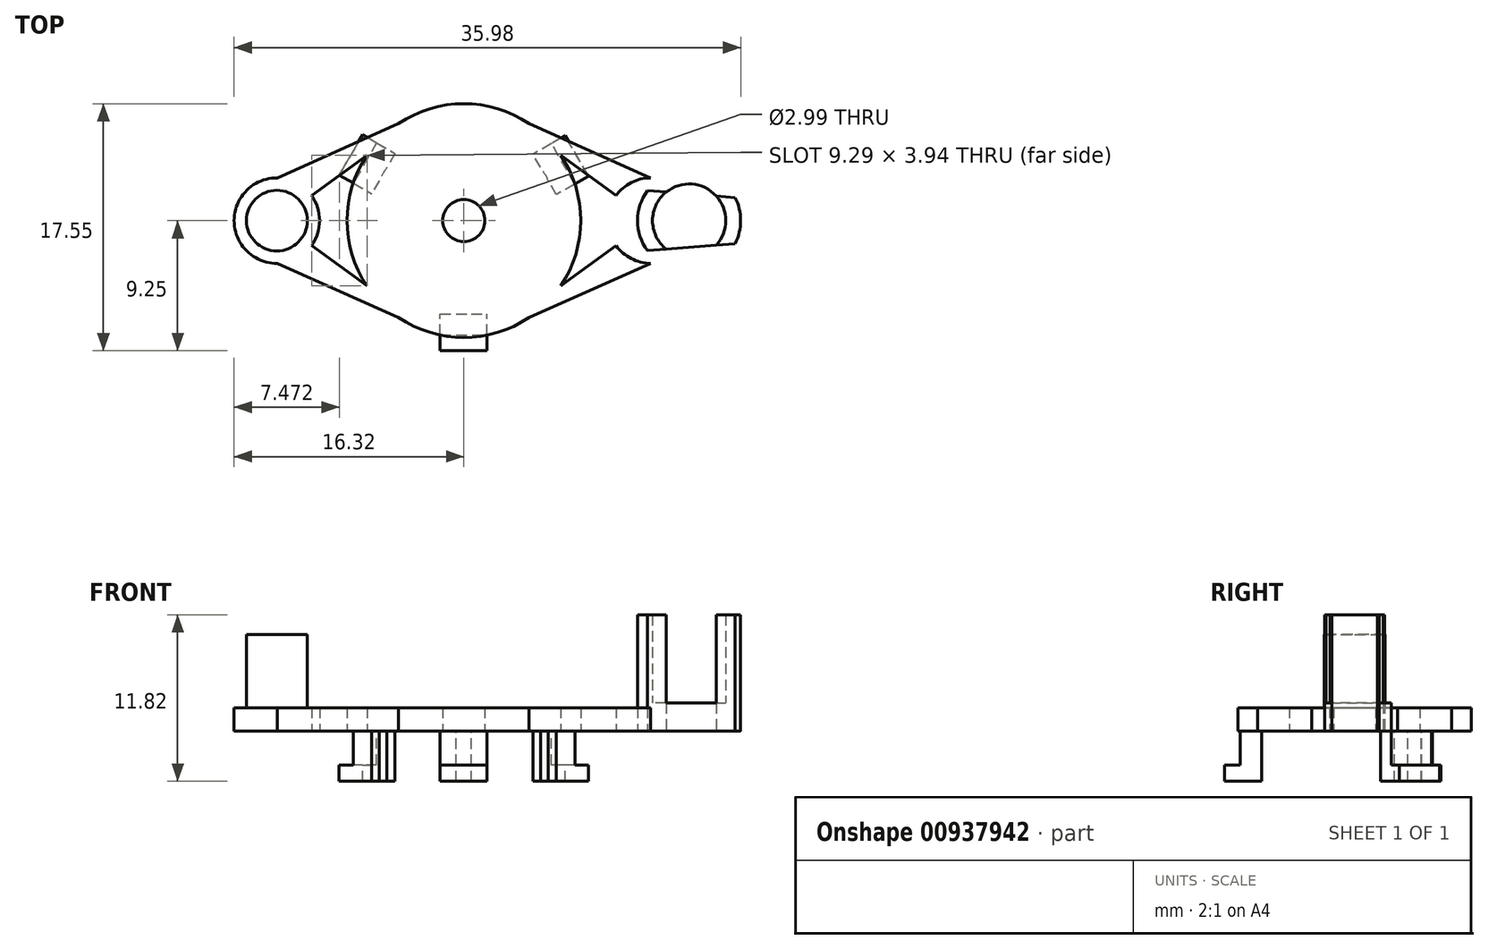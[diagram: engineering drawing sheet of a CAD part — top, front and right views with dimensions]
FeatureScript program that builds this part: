
annotation { "Feature Type Name" : "Feature", "Feature Type Description" : "" }
export const myFeature = defineFeature(function(context is Context, id is Id, definition is map)
    precondition{}
    {
        {
            var Q0;
            Q0=qCreatedBy(makeId("Top.planeOp"),FACE);
            var sketch = newSketch(context, id + "F0", { "sketchPlane" : qUnion([Q0])});
            skPoint(sketch, "E0.middle", {"position": v(0, 0) * mm});
            skCircle(sketch, "E1", {"center": v(-16, 0) * mm, "radius": 2.6 * mm});
            skCircle(sketch, "E2.MirrorC", {"center": v(16, 0) * mm, "radius": 2.6 * mm});
            skCircle(sketch, "E3", {"center": v(0, 0) * mm, "radius": 1.8 * mm});
            skCircle(sketch, "E4", {"center": v(-16, 0) * mm, "radius": 3.66 * mm});
            skCircle(sketch, "E5.MirrorC", {"center": v(16, 0) * mm, "radius": 3.66 * mm});
            skCircle(sketch, "E6", {"center": v(0, 0) * mm, "radius": 10 * mm});
            skLineSegment(sketch, "E7", {"start": v(-19.27, 1.63) * mm, "end": v(-9.7, 2.4) * mm});
            skLineSegment(sketch, "E8.MirrorCS", {"start": v(-19.27, -1.63) * mm, "end": v(-9.7, -2.4) * mm});
            skLineSegment(sketch, "E9.MirrorCS", {"start": v(19.27, 1.63) * mm, "end": v(9.7, 2.4) * mm});
            skLineSegment(sketch, "E10.MirrorCS", {"start": v(19.27, -1.63) * mm, "end": v(9.7, -2.4) * mm});
            skLineSegment(sketch, "E11", {"start": v(-15.97, 3.66) * mm, "end": v(-5.58, 8.3) * mm});
            skLineSegment(sketch, "E12", {"start": v(-13.03, 2.14) * mm, "end": v(-8.29, 5.6) * mm});
            skLineSegment(sketch, "E13.MirrorCS", {"start": v(-13.03, -2.14) * mm, "end": v(-8.29, -5.6) * mm});
            skLineSegment(sketch, "E14.MirrorCS", {"start": v(-15.97, -3.66) * mm, "end": v(-5.58, -8.3) * mm});
            skLineSegment(sketch, "E15.MirrorCS", {"start": v(13.03, 2.14) * mm, "end": v(8.29, 5.6) * mm});
            skLineSegment(sketch, "E16.MirrorCS", {"start": v(15.97, 3.66) * mm, "end": v(5.58, 8.3) * mm});
            skLineSegment(sketch, "E17.MirrorCS", {"start": v(15.97, -3.66) * mm, "end": v(5.58, -8.3) * mm});
            skLineSegment(sketch, "E18.MirrorCS", {"start": v(13.03, -2.14) * mm, "end": v(8.29, -5.6) * mm});
            skCircle(sketch, "E19", {"center": v(0, 0) * mm, "radius": 8 * mm});
            skLineSegment(sketch, "E20.bottom", {"start": v(-2.04, -9.79) * mm, "end": v(1.96, -9.79) * mm});
            skLineSegment(sketch, "E20.top", {"start": v(-2.04, -7.97) * mm, "end": v(1.96, -7.97) * mm});
            skLineSegment(sketch, "E20.left", {"start": v(-2.04, -9.79) * mm, "end": v(-2.04, -7.97) * mm});
            skLineSegment(sketch, "E20.right", {"start": v(1.96, -9.79) * mm, "end": v(1.96, -7.97) * mm});
            skLineSegment(sketch, "E21.1.0", {"start": v(9.5, 3.13) * mm, "end": v(7.5, 6.6) * mm});
            skLineSegment(sketch, "E21.1.1", {"start": v(7.5, 6.6) * mm, "end": v(5.92, 5.68) * mm});
            skLineSegment(sketch, "E21.1.2", {"start": v(7.92, 2.22) * mm, "end": v(5.92, 5.68) * mm});
            skLineSegment(sketch, "E21.1.3", {"start": v(9.5, 3.13) * mm, "end": v(7.92, 2.22) * mm});
            skLineSegment(sketch, "E21.2.0", {"start": v(-7.46, 6.66) * mm, "end": v(-9.46, 3.2) * mm});
            skLineSegment(sketch, "E21.2.1", {"start": v(-9.46, 3.2) * mm, "end": v(-7.89, 2.29) * mm});
            skLineSegment(sketch, "E21.2.2", {"start": v(-5.89, 5.75) * mm, "end": v(-7.89, 2.29) * mm});
            skLineSegment(sketch, "E21.2.3", {"start": v(-7.46, 6.66) * mm, "end": v(-5.89, 5.75) * mm});
            skSolve(sketch);
        }
        {
            var Q0;
            {var subQ0=sQuery(id+"F0.wireOp",EDGE,"E11");Q0=makeQuery(id+"F0.imprint","IMPRINT",FACE,{"disambiguationData":[TD([[makeQuery(id+"F0.imprint","IMPRINT",EDGE,{"derivedFrom":subQ0}),-1.0]])]});}
            var Q1;
            Q1=makeQuery(id+"F0.imprint","IMPRINT",FACE,{"disambiguationData":[TD([[makeQuery(id+"F0.imprint","IMPRINT",EDGE,{"derivedFrom":sQuery(id+"F0.wireOp",EDGE,"E3")}),-1.0]])]});
            var Q2;
            {var subQ0=sQuery(id+"F0.wireOp",EDGE,"E13.MirrorCS");Q2=makeQuery(id+"F0.imprint","IMPRINT",FACE,{"disambiguationData":[TD([[makeQuery(id+"F0.imprint","IMPRINT",EDGE,{"derivedFrom":subQ0}),-1.0]])]});}
            var Q3;
            {var subQ0=sQuery(id+"F0.wireOp",EDGE,"E8.MirrorCS");var subQ3=sQuery(id+"F0.wireOp",EDGE,"E1");var subQ4=makeQuery(id+"F0.imprint","INTERSECT",VERTEX,{"disambiguationData":[OD(0.0)],"derivedFrom":[subQ3,subQ0]});Q3=makeQuery(id+"F0.imprint","IMPRINT",FACE,{"disambiguationData":[TD([[makeQuery(id+"F0.imprint","IMPRINT",EDGE,{"disambiguationData":[TD([[subQ4,-1.0]])],"derivedFrom":subQ3}),-1.0]])]});}
            var Q4;
            {var subQ0=sQuery(id+"F0.wireOp",EDGE,"E7");var subQ1=sQuery(id+"F0.wireOp",EDGE,"E1");var subQ2=makeQuery(id+"F0.imprint","INTERSECT",VERTEX,{"disambiguationData":[OD(0.0)],"derivedFrom":[subQ1,subQ0]});Q4=makeQuery(id+"F0.imprint","IMPRINT",FACE,{"disambiguationData":[TD([[makeQuery(id+"F0.imprint","IMPRINT",EDGE,{"disambiguationData":[TD([[subQ2,-1.0]])],"derivedFrom":subQ1}),-1.0]])]});}
            var Q5;
            {var subQ0=sQuery(id+"F0.wireOp",EDGE,"E7");var subQ3=sQuery(id+"F0.wireOp",EDGE,"E1");var subQ4=makeQuery(id+"F0.imprint","INTERSECT",VERTEX,{"disambiguationData":[OD(0.0)],"derivedFrom":[subQ3,subQ0]});Q5=makeQuery(id+"F0.imprint","IMPRINT",FACE,{"disambiguationData":[TD([[makeQuery(id+"F0.imprint","IMPRINT",EDGE,{"disambiguationData":[TD([[subQ4,1.0]])],"derivedFrom":subQ3}),-1.0]])]});}
            var Q6;
            {var subQ0=sQuery(id+"F0.wireOp",EDGE,"E7");var subQ1=sQuery(id+"F0.wireOp",EDGE,"E1");var subQ2=makeQuery(id+"F0.imprint","INTERSECT",VERTEX,{"disambiguationData":[OD(1.0)],"derivedFrom":[subQ1,subQ0]});Q6=makeQuery(id+"F0.imprint","IMPRINT",FACE,{"disambiguationData":[TD([[makeQuery(id+"F0.imprint","IMPRINT",EDGE,{"disambiguationData":[TD([[subQ2,1.0]])],"derivedFrom":subQ1}),-1.0]])]});}
            var Q7;
            {var subQ0=sQuery(id+"F0.wireOp",EDGE,"E17.MirrorCS");Q7=makeQuery(id+"F0.imprint","IMPRINT",FACE,{"disambiguationData":[TD([[makeQuery(id+"F0.imprint","IMPRINT",EDGE,{"derivedFrom":subQ0}),-1.0]])]});}
            var Q8;
            {var subQ0=sQuery(id+"F0.wireOp",EDGE,"E15.MirrorCS");Q8=makeQuery(id+"F0.imprint","IMPRINT",FACE,{"disambiguationData":[TD([[makeQuery(id+"F0.imprint","IMPRINT",EDGE,{"derivedFrom":subQ0}),-1.0]])]});}
            var Q9;
            {var subQ0=sQuery(id+"F0.wireOp",EDGE,"E9.MirrorCS");var subQ3=sQuery(id+"F0.wireOp",EDGE,"E2.MirrorC");var subQ4=makeQuery(id+"F0.imprint","INTERSECT",VERTEX,{"disambiguationData":[OD(0.0)],"derivedFrom":[subQ3,subQ0]});Q9=makeQuery(id+"F0.imprint","IMPRINT",FACE,{"disambiguationData":[TD([[makeQuery(id+"F0.imprint","IMPRINT",EDGE,{"disambiguationData":[TD([[subQ4,1.0]])],"derivedFrom":subQ3}),1.0]])]});}
            var Q10;
            {var subQ0=sQuery(id+"F0.wireOp",EDGE,"E9.MirrorCS");var subQ1=sQuery(id+"F0.wireOp",EDGE,"E2.MirrorC");var subQ2=makeQuery(id+"F0.imprint","INTERSECT",VERTEX,{"disambiguationData":[OD(1.0)],"derivedFrom":[subQ1,subQ0]});Q10=makeQuery(id+"F0.imprint","IMPRINT",FACE,{"disambiguationData":[TD([[makeQuery(id+"F0.imprint","IMPRINT",EDGE,{"disambiguationData":[TD([[subQ2,1.0]])],"derivedFrom":subQ1}),1.0]])]});}
            var Q11;
            {var subQ0=sQuery(id+"F0.wireOp",EDGE,"E10.MirrorCS");var subQ3=sQuery(id+"F0.wireOp",EDGE,"E2.MirrorC");var subQ4=makeQuery(id+"F0.imprint","INTERSECT",VERTEX,{"disambiguationData":[OD(0.0)],"derivedFrom":[subQ3,subQ0]});Q11=makeQuery(id+"F0.imprint","IMPRINT",FACE,{"disambiguationData":[TD([[makeQuery(id+"F0.imprint","IMPRINT",EDGE,{"disambiguationData":[TD([[subQ4,-1.0]])],"derivedFrom":subQ3}),1.0]])]});}
            var Q12;
            {var subQ0=sQuery(id+"F0.wireOp",EDGE,"E9.MirrorCS");var subQ1=sQuery(id+"F0.wireOp",EDGE,"E2.MirrorC");var subQ2=makeQuery(id+"F0.imprint","INTERSECT",VERTEX,{"disambiguationData":[OD(0.0)],"derivedFrom":[subQ1,subQ0]});Q12=makeQuery(id+"F0.imprint","IMPRINT",FACE,{"disambiguationData":[TD([[makeQuery(id+"F0.imprint","IMPRINT",EDGE,{"disambiguationData":[TD([[subQ2,-1.0]])],"derivedFrom":subQ1}),1.0]])]});}
            var Q13;
            {var subQ0=sQuery(id+"F0.wireOp",EDGE,"E6");var subQ8=makeQuery(id+"F0.imprint","INTERSECT",VERTEX,{"derivedFrom":[subQ0,sQuery(id+"F0.wireOp",EDGE,"E9.MirrorCS")]});Q13=makeQuery(id+"F0.imprint","IMPRINT",FACE,{"disambiguationData":[TD([[makeQuery(id+"F0.imprint","IMPRINT",EDGE,{"disambiguationData":[TD([[subQ8,-1.0]])],"derivedFrom":subQ0}),1.0]])]});}
            var Q14;
            {var subQ0=sQuery(id+"F0.wireOp",EDGE,"E20.left");Q14=makeQuery(id+"F0.imprint","IMPRINT",FACE,{"disambiguationData":[TD([[makeQuery(id+"F0.imprint","IMPRINT",EDGE,{"derivedFrom":subQ0}),1.0]])]});}
            var Q15;
            {var subQ7=sQuery(id+"F0.wireOp",EDGE,"E21.1.3");Q15=makeQuery(id+"F0.imprint","IMPRINT",FACE,{"disambiguationData":[TD([[makeQuery(id+"F0.imprint","IMPRINT",EDGE,{"derivedFrom":subQ7}),1.0]])]});}
            var Q16;
            {var subQ5=sQuery(id+"F0.wireOp",EDGE,"E21.2.3");Q16=makeQuery(id+"F0.imprint","IMPRINT",FACE,{"disambiguationData":[TD([[makeQuery(id+"F0.imprint","IMPRINT",EDGE,{"derivedFrom":subQ5}),1.0]])]});}
            var Q17;
            {var subQ0=sQuery(id+"F0.wireOp",EDGE,"E20.bottom");var subQ1=sQuery(id+"F0.wireOp",EDGE,"E6");var subQ3=makeQuery(id+"F0.imprint","INTERSECT",VERTEX,{"derivedFrom":[subQ1,subQ0]});Q17=makeQuery(id+"F0.imprint","IMPRINT",FACE,{"disambiguationData":[TD([[makeQuery(id+"F0.imprint","IMPRINT",EDGE,{"disambiguationData":[TD([[subQ3,1.0]])],"derivedFrom":subQ1}),1.0]])]});}
            var Q18;
            {var subQ0=sQuery(id+"F0.wireOp",EDGE,"E21.1.0");var subQ1=sQuery(id+"F0.wireOp",EDGE,"E6");var subQ3=makeQuery(id+"F0.imprint","INTERSECT",VERTEX,{"derivedFrom":[subQ1,subQ0]});Q18=makeQuery(id+"F0.imprint","IMPRINT",FACE,{"disambiguationData":[TD([[makeQuery(id+"F0.imprint","IMPRINT",EDGE,{"disambiguationData":[TD([[subQ3,1.0]])],"derivedFrom":subQ1}),1.0]])]});}
            var Q19;
            {var subQ0=sQuery(id+"F0.wireOp",EDGE,"E21.2.0");var subQ1=sQuery(id+"F0.wireOp",EDGE,"E6");var subQ3=makeQuery(id+"F0.imprint","INTERSECT",VERTEX,{"derivedFrom":[subQ1,subQ0]});Q19=makeQuery(id+"F0.imprint","IMPRINT",FACE,{"disambiguationData":[TD([[makeQuery(id+"F0.imprint","IMPRINT",EDGE,{"disambiguationData":[TD([[subQ3,1.0]])],"derivedFrom":subQ1}),1.0]])]});}
            var Q20;
            {var subQ0=sQuery(id+"F0.wireOp",EDGE,"E20.left");Q20=makeQuery(id+"F0.imprint","IMPRINT",FACE,{"disambiguationData":[TD([[makeQuery(id+"F0.imprint","IMPRINT",EDGE,{"derivedFrom":subQ0}),-1.0]])]});}
            var Q21;
            {var subQ5=sQuery(id+"F0.wireOp",EDGE,"E21.2.3");Q21=makeQuery(id+"F0.imprint","IMPRINT",FACE,{"disambiguationData":[TD([[makeQuery(id+"F0.imprint","IMPRINT",EDGE,{"derivedFrom":subQ5}),-1.0]])]});}
            var Q22;
            {var subQ5=sQuery(id+"F0.wireOp",EDGE,"E21.1.3");Q22=makeQuery(id+"F0.imprint","IMPRINT",FACE,{"disambiguationData":[TD([[makeQuery(id+"F0.imprint","IMPRINT",EDGE,{"derivedFrom":subQ5}),-1.0]])]});}
            var Q23;
            {var subQ0=sQuery(id+"F0.wireOp",EDGE,"E20.top");var subQ1=sQuery(id+"F0.wireOp",EDGE,"E19");var subQ2=makeQuery(id+"F0.imprint","INTERSECT",VERTEX,{"disambiguationData":[OD(0.0)],"derivedFrom":[subQ1,subQ0]});Q23=makeQuery(id+"F0.imprint","IMPRINT",FACE,{"disambiguationData":[TD([[makeQuery(id+"F0.imprint","IMPRINT",EDGE,{"disambiguationData":[TD([[subQ2,-1.0]])],"derivedFrom":subQ1}),1.0]])]});}
            var Q24;
            {var subQ0=sQuery(id+"F0.wireOp",EDGE,"E21.2.2");var subQ1=sQuery(id+"F0.wireOp",EDGE,"E19");var subQ2=makeQuery(id+"F0.imprint","INTERSECT",VERTEX,{"disambiguationData":[OD(0.0)],"derivedFrom":[subQ1,subQ0]});Q24=makeQuery(id+"F0.imprint","IMPRINT",FACE,{"disambiguationData":[TD([[makeQuery(id+"F0.imprint","IMPRINT",EDGE,{"disambiguationData":[TD([[subQ2,-1.0]])],"derivedFrom":subQ1}),1.0]])]});}
            var Q25;
            {var subQ0=sQuery(id+"F0.wireOp",EDGE,"E21.1.2");var subQ1=sQuery(id+"F0.wireOp",EDGE,"E19");var subQ2=makeQuery(id+"F0.imprint","INTERSECT",VERTEX,{"disambiguationData":[OD(0.0)],"derivedFrom":[subQ1,subQ0]});Q25=makeQuery(id+"F0.imprint","IMPRINT",FACE,{"disambiguationData":[TD([[makeQuery(id+"F0.imprint","IMPRINT",EDGE,{"disambiguationData":[TD([[subQ2,1.0]])],"derivedFrom":subQ1}),1.0]])]});}
            extrude(context, id + "F1", {"entities" : qUnion([Q0, Q1, Q2, Q3, Q4, Q5, Q6, Q7, Q8, Q9, Q10, Q11, Q12, Q13, Q14, Q15, Q16, Q17, Q18, Q19, Q20, Q21, Q22, Q23, Q24, Q25]), "depth" : 2 * mm, "offsetDistance" : 25 * mm});
        }
        {
            var Q0;
            Q0=makeQuery(id+"F0.imprint","IMPRINT",FACE,{"disambiguationData":[TD([[makeQuery(id+"F0.imprint","IMPRINT",EDGE,{"derivedFrom":sQuery(id+"F0.wireOp",EDGE,"E1")}),1.0]])]});
            var Q1;
            Q1=makeQuery(id+"F0.imprint","IMPRINT",FACE,{"disambiguationData":[TD([[makeQuery(id+"F0.imprint","IMPRINT",EDGE,{"derivedFrom":sQuery(id+"F0.wireOp",EDGE,"E2.MirrorC")}),-1.0]])]});
            var Q2;
            {var subQ0=sQuery(id+"F0.wireOp",EDGE,"E7");var subQ1=sQuery(id+"F0.wireOp",EDGE,"E1");var subQ2=makeQuery(id+"F0.imprint","INTERSECT",VERTEX,{"disambiguationData":[OD(0.0)],"derivedFrom":[subQ1,subQ0]});Q2=makeQuery(id+"F0.imprint","IMPRINT",FACE,{"disambiguationData":[TD([[makeQuery(id+"F0.imprint","IMPRINT",EDGE,{"disambiguationData":[TD([[subQ2,1.0]])],"derivedFrom":subQ1}),1.0]])]});}
            var Q3;
            {var subQ0=sQuery(id+"F0.wireOp",EDGE,"E8.MirrorCS");var subQ1=sQuery(id+"F0.wireOp",EDGE,"E1");var subQ2=makeQuery(id+"F0.imprint","INTERSECT",VERTEX,{"disambiguationData":[OD(0.0)],"derivedFrom":[subQ1,subQ0]});Q3=makeQuery(id+"F0.imprint","IMPRINT",FACE,{"disambiguationData":[TD([[makeQuery(id+"F0.imprint","IMPRINT",EDGE,{"disambiguationData":[TD([[subQ2,-1.0]])],"derivedFrom":subQ1}),1.0]])]});}
            var Q4;
            {var subQ0=sQuery(id+"F0.wireOp",EDGE,"E10.MirrorCS");var subQ1=sQuery(id+"F0.wireOp",EDGE,"E2.MirrorC");var subQ2=makeQuery(id+"F0.imprint","INTERSECT",VERTEX,{"disambiguationData":[OD(0.0)],"derivedFrom":[subQ1,subQ0]});Q4=makeQuery(id+"F0.imprint","IMPRINT",FACE,{"disambiguationData":[TD([[makeQuery(id+"F0.imprint","IMPRINT",EDGE,{"disambiguationData":[TD([[subQ2,-1.0]])],"derivedFrom":subQ1}),-1.0]])]});}
            var Q5;
            {var subQ0=sQuery(id+"F0.wireOp",EDGE,"E9.MirrorCS");var subQ1=sQuery(id+"F0.wireOp",EDGE,"E2.MirrorC");var subQ2=makeQuery(id+"F0.imprint","INTERSECT",VERTEX,{"disambiguationData":[OD(0.0)],"derivedFrom":[subQ1,subQ0]});Q5=makeQuery(id+"F0.imprint","IMPRINT",FACE,{"disambiguationData":[TD([[makeQuery(id+"F0.imprint","IMPRINT",EDGE,{"disambiguationData":[TD([[subQ2,1.0]])],"derivedFrom":subQ1}),-1.0]])]});}
            extrude(context, id + "F2", {"entities" : qUnion([Q0, Q1, Q2, Q3, Q4, Q5]), "operationType" : NewBodyOperationType.ADD, "depth" : 8.25 * mm, "offsetDistance" : 25 * mm});
        }
        {
            var Q0;
            {var subQ5=sQuery(id+"F0.wireOp",EDGE,"E21.2.3");Q0=makeQuery(id+"F0.imprint","IMPRINT",FACE,{"disambiguationData":[TD([[makeQuery(id+"F0.imprint","IMPRINT",EDGE,{"derivedFrom":subQ5}),-1.0]])]});}
            var Q1;
            {var subQ5=sQuery(id+"F0.wireOp",EDGE,"E21.1.3");Q1=makeQuery(id+"F0.imprint","IMPRINT",FACE,{"disambiguationData":[TD([[makeQuery(id+"F0.imprint","IMPRINT",EDGE,{"derivedFrom":subQ5}),-1.0]])]});}
            var Q2;
            {var subQ0=sQuery(id+"F0.wireOp",EDGE,"E20.left");Q2=makeQuery(id+"F0.imprint","IMPRINT",FACE,{"disambiguationData":[TD([[makeQuery(id+"F0.imprint","IMPRINT",EDGE,{"derivedFrom":subQ0}),-1.0]])]});}
            extrude(context, id + "F3", {"entities" : qUnion([Q0, Q1, Q2]), "operationType" : NewBodyOperationType.ADD, "oppositeDirection" : true, "depth" : 4.3 * mm, "offsetDistance" : 25 * mm});
        }
        {
            var Q0;
            Q0=makeQuery(id+"F3.opExtrude","SWEPT_FACE",FACE,{"disambiguationData":[OSD([sQuery(id+"F0.wireOp",EDGE,"E20.bottom")])]});
            var sketch = newSketch(context, id + "F4", { "sketchPlane" : qUnion([Q0])});
            skLineSegment(sketch, "E22.bottom", {"start": v(-2.04, -4.3) * mm, "end": v(-2.04, -4.3) * mm});
            skLineSegment(sketch, "E22.top", {"start": v(-2.04, -2.9) * mm, "end": v(-2.04, -2.9) * mm});
            skLineSegment(sketch, "E22.left", {"start": v(-2.04, -4.3) * mm, "end": v(-2.04, -2.9) * mm});
            skLineSegment(sketch, "E22.right", {"start": v(-2.04, -4.3) * mm, "end": v(-2.04, -2.9) * mm});
            skLineSegment(sketch, "E23", {"start": v(-2.04, -2.9) * mm, "end": v(1.96, -2.9) * mm});
            skLineSegment(sketch, "E24", {"start": v(1.96, -2.9) * mm, "end": v(1.96, -4.3) * mm});
            skLineSegment(sketch, "E25", {"start": v(1.96, -4.3) * mm, "end": v(-2.04, -4.3) * mm});
            skSolve(sketch);
        }
        {
            var Q0;
            Q0 = qSketchRegion(id + "F4", true);
            extrude(context, id + "F5", {"entities" : qUnion([Q0]), "operationType" : NewBodyOperationType.ADD, "depth" : 1.35 * mm, "offsetDistance" : 25 * mm});
        }
        {
            var Q0;
            Q0=makeQuery(id+"F3.opExtrude","SWEPT_FACE",FACE,{"disambiguationData":[OSD([sQuery(id+"F0.wireOp",EDGE,"E21.2.0")])]});
            var sketch = newSketch(context, id + "F6", { "sketchPlane" : qUnion([Q0])});
            skLineSegment(sketch, "E26.bottom", {"start": v(-2.04, -4.3) * mm, "end": v(-2.04, -4.3) * mm});
            skLineSegment(sketch, "E26.top", {"start": v(-2.04, -2.9) * mm, "end": v(-2.04, -2.9) * mm});
            skLineSegment(sketch, "E26.left", {"start": v(-2.04, -4.3) * mm, "end": v(-2.04, -2.9) * mm});
            skLineSegment(sketch, "E26.right", {"start": v(-2.04, -4.3) * mm, "end": v(-2.04, -2.9) * mm});
            skLineSegment(sketch, "E27", {"start": v(-2.04, -2.9) * mm, "end": v(1.96, -2.9) * mm});
            skLineSegment(sketch, "E28", {"start": v(1.96, -2.9) * mm, "end": v(1.96, -4.3) * mm});
            skLineSegment(sketch, "E29", {"start": v(1.96, -4.3) * mm, "end": v(-2.04, -4.3) * mm});
            skSolve(sketch);
        }
        {
            var Q0;
            Q0 = qSketchRegion(id + "F6", true);
            extrude(context, id + "F7", {"entities" : qUnion([Q0]), "operationType" : NewBodyOperationType.ADD, "depth" : 1.4 * mm, "offsetDistance" : 25 * mm});
        }
        {
            var Q0;
            Q0=makeQuery(id+"F3.opExtrude","SWEPT_FACE",FACE,{"disambiguationData":[OSD([sQuery(id+"F0.wireOp",EDGE,"E21.1.0")])]});
            var sketch = newSketch(context, id + "F8", { "sketchPlane" : qUnion([Q0])});
            skLineSegment(sketch, "E30.bottom", {"start": v(-2.04, -4.3) * mm, "end": v(-2.04, -4.3) * mm});
            skLineSegment(sketch, "E30.top", {"start": v(-2.04, -2.9) * mm, "end": v(-2.04, -2.9) * mm});
            skLineSegment(sketch, "E30.left", {"start": v(-2.04, -4.3) * mm, "end": v(-2.04, -2.9) * mm});
            skLineSegment(sketch, "E30.right", {"start": v(-2.04, -4.3) * mm, "end": v(-2.04, -2.9) * mm});
            skLineSegment(sketch, "E31", {"start": v(-2.04, -2.9) * mm, "end": v(1.96, -2.9) * mm});
            skLineSegment(sketch, "E32", {"start": v(1.96, -2.9) * mm, "end": v(1.96, -4.3) * mm});
            skLineSegment(sketch, "E33", {"start": v(1.96, -4.3) * mm, "end": v(-2.04, -4.3) * mm});
            skSolve(sketch);
        }
        {
            var Q0;
            Q0 = qSketchRegion(id + "F8", true);
            extrude(context, id + "F9", {"entities" : qUnion([Q0]), "operationType" : NewBodyOperationType.ADD, "depth" : 1.35 * mm, "offsetDistance" : 25 * mm});
        }
        {
            var Q0;
            Q0=makeQuery(id+"F1.opExtrude","SWEPT_BODY",BODY,{"disambiguationData":[OSD([sQuery(id+"F0.wireOp",EDGE,"E1"),sQuery(id+"F0.wireOp",EDGE,"E2.MirrorC"),sQuery(id+"F0.wireOp",EDGE,"E3"),sQuery(id+"F0.wireOp",EDGE,"E4"),sQuery(id+"F0.wireOp",EDGE,"E5.MirrorC"),sQuery(id+"F0.wireOp",EDGE,"E6"),sQuery(id+"F0.wireOp",EDGE,"E11"),sQuery(id+"F0.wireOp",EDGE,"E12"),sQuery(id+"F0.wireOp",EDGE,"E13.MirrorCS"),sQuery(id+"F0.wireOp",EDGE,"E14.MirrorCS"),sQuery(id+"F0.wireOp",EDGE,"E15.MirrorCS"),sQuery(id+"F0.wireOp",EDGE,"E16.MirrorCS"),sQuery(id+"F0.wireOp",EDGE,"E17.MirrorCS"),sQuery(id+"F0.wireOp",EDGE,"E18.MirrorCS"),sQuery(id+"F0.wireOp",EDGE,"E6"),sQuery(id+"F0.wireOp",EDGE,"E20.bottom"),sQuery(id+"F0.wireOp",EDGE,"E20.right"),sQuery(id+"F0.wireOp",EDGE,"E21.1.0"),sQuery(id+"F0.wireOp",EDGE,"E21.1.1"),sQuery(id+"F0.wireOp",EDGE,"E21.2.0"),sQuery(id+"F0.wireOp",EDGE,"E21.2.1")])]});
            var Q1;
            Q1=sQuery(id+"F0.wireOp",VERTEX,"E0.middle");
            transform(context, id + "F10", {"entities" : qUnion([Q0]), "transformType" : TransformType.SCALE_UNIFORMLY, "scale" : .83, "scalePoint" : qUnion([Q1]), "makeCopy" : false});
        }
    });
